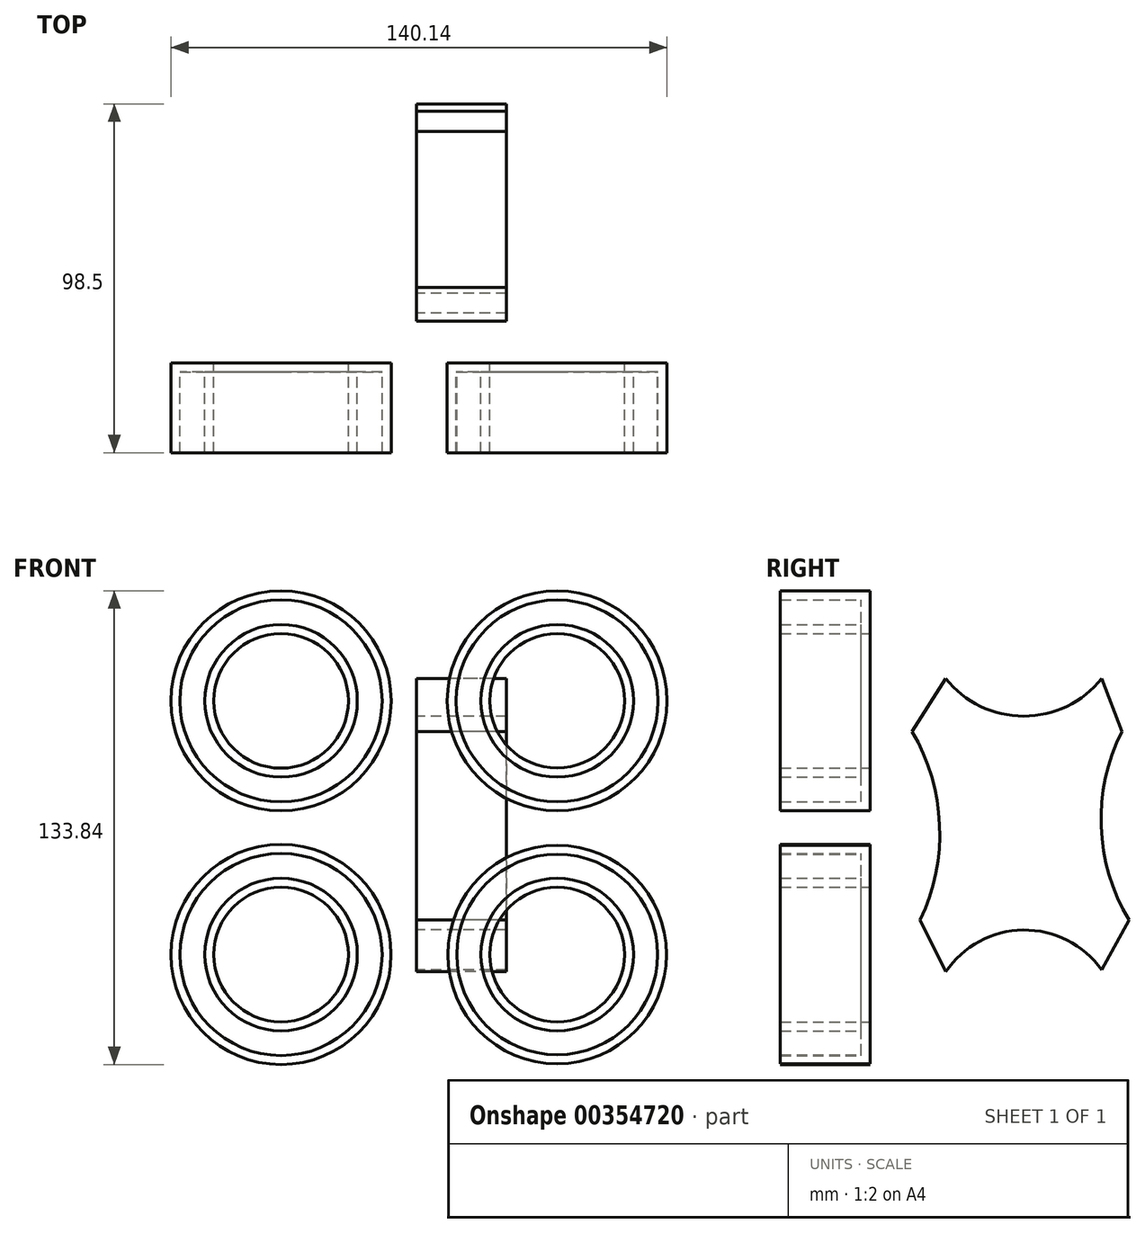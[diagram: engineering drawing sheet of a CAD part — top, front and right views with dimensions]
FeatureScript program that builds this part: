
annotation { "Feature Type Name" : "Feature", "Feature Type Description" : "" }
export const myFeature = defineFeature(function(context is Context, id is Id, definition is map)
    precondition{}
    {
        {
            var Q0;
            Q0=qCreatedBy(makeId("Front.planeOp"),FACE);
            var sketch = newSketch(context, id + "F0", { "sketchPlane" : qUnion([Q0])});
            skCircle(sketch, "E0", {"center": v(-38.28, 37.41) * mm, "radius": 31.1 * mm});
            skCircle(sketch, "E1", {"center": v(39.72, 37.41) * mm, "radius": 31.06 * mm});
            skCircle(sketch, "E2", {"center": v(39.72, -34.25) * mm, "radius": 30.88 * mm});
            skCircle(sketch, "E3", {"center": v(-38.28, -34.25) * mm, "radius": 31.08 * mm});
            skCircle(sketch, "E4", {"center": v(-38.28, 37.41) * mm, "radius": 19.01 * mm});
            skCircle(sketch, "E5", {"center": v(39.72, 37.41) * mm, "radius": 19 * mm});
            skCircle(sketch, "E6", {"center": v(39.72, -34.25) * mm, "radius": 19.01 * mm});
            skCircle(sketch, "E7", {"center": v(-38.28, -34.25) * mm, "radius": 19.01 * mm});
            skSolve(sketch);
        }
        {
            var Q0;
            Q0=qSketchRegion(id+"F0",true);
            extrude(context, id + "F1", {"entities" : qUnion([Q0]), "depth" : 25.4 * mm});
        }
        {
            var Q0;
            Q0=makeQuery(id+"F1.opExtrude","CAP_FACE",FACE,{"disambiguationData":[OSD([sQuery(id+"F0.wireOp",EDGE,"E0"),sQuery(id+"F0.wireOp",EDGE,"E4")])],"isStart":false});
            var Q1;
            Q1=makeQuery(id+"F1.opExtrude","CAP_FACE",FACE,{"disambiguationData":[OSD([sQuery(id+"F0.wireOp",EDGE,"E1"),sQuery(id+"F0.wireOp",EDGE,"E5")])],"isStart":false});
            var Q2;
            Q2=makeQuery(id+"F1.opExtrude","CAP_FACE",FACE,{"disambiguationData":[OSD([sQuery(id+"F0.wireOp",EDGE,"E2"),sQuery(id+"F0.wireOp",EDGE,"E6")])],"isStart":false});
            var Q3;
            Q3=makeQuery(id+"F1.opExtrude","CAP_FACE",FACE,{"disambiguationData":[OSD([sQuery(id+"F0.wireOp",EDGE,"E3"),sQuery(id+"F0.wireOp",EDGE,"E7")])],"isStart":false});
            shell(context, id + "F2", {"entities" : qUnion([Q0, Q1, Q2, Q3]), "thickness" : 2.54 * mm});
        }
        {
            var Q0;
            Q0=qCreatedBy(makeId("Right.planeOp"),FACE);
            var sketch = newSketch(context, id + "F3", { "sketchPlane" : qUnion([Q0])});
            skArc(sketch, "E8", {"start": v(21.3, 43.75) * mm, "mid": v(43.31, 33.1) * mm, "end": v(65.33, 43.75) * mm});
            skArc(sketch, "E9", {"start": v(65.33, -38.57) * mm, "mid": v(43.16, -27.32) * mm, "end": v(21.3, -39.14) * mm});
            skArc(sketch, "E10", {"start": v(14.1, -24.46) * mm, "mid": v(19.56, 2.44) * mm, "end": v(11.8, 28.78) * mm});
            skArc(sketch, "E11", {"start": v(71.09, 28.78) * mm, "mid": v(65.2, 1.9) * mm, "end": v(73.1, -24.46) * mm});
            skLineSegment(sketch, "E12", {"start": v(14.1, -24.46) * mm, "end": v(21.3, -39.14) * mm});
            skLineSegment(sketch, "E13", {"start": v(65.33, -38.57) * mm, "end": v(73.1, -24.46) * mm});
            skLineSegment(sketch, "E14", {"start": v(71.09, 28.78) * mm, "end": v(65.33, 43.75) * mm});
            skLineSegment(sketch, "E15", {"start": v(11.8, 28.78) * mm, "end": v(21.3, 43.75) * mm});
            skSolve(sketch);
        }
        {
            var Q0;
            Q0=qSketchRegion(id+"F3",true);
            extrude(context, id + "F4", {"entities" : qUnion([Q0]), "depth" : 25.4 * mm});
        }
    });
